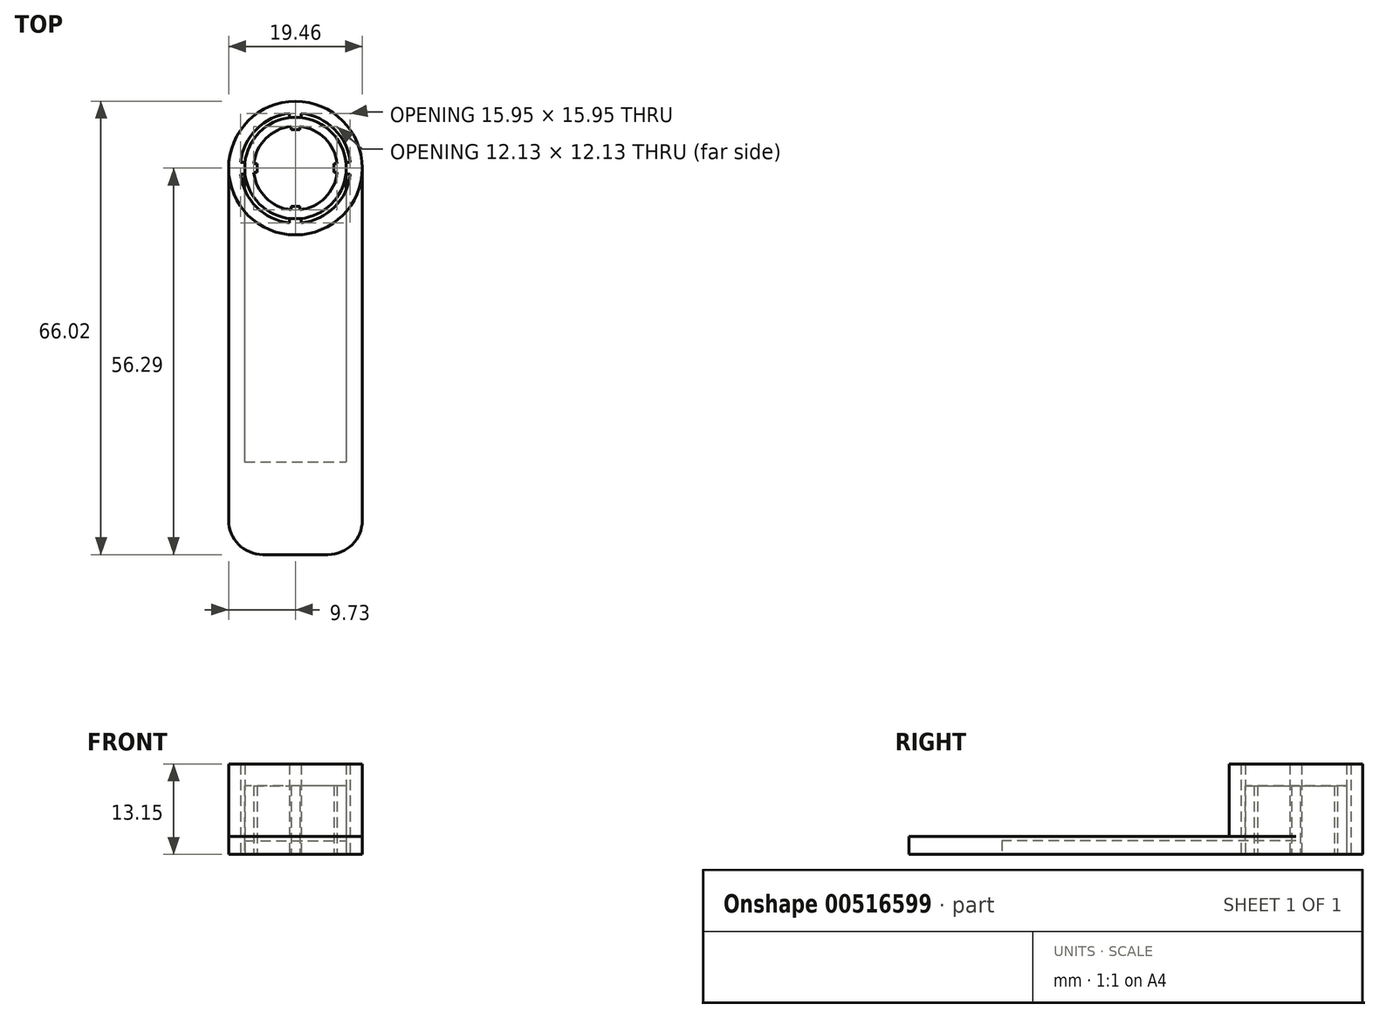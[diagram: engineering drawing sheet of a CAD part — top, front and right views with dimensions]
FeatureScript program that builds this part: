
annotation { "Feature Type Name" : "Feature", "Feature Type Description" : "" }
export const myFeature = defineFeature(function(context is Context, id is Id, definition is map)
    precondition{}
    {
        {
            var Q0;
            Q0=qCreatedBy(makeId("Top.planeOp"),FACE);
            var sketch = newSketch(context, id + "F0", { "sketchPlane" : qUnion([Q0])});
            skArc(sketch, "E0", {"start": v(0.65, -6.07) * mm, "mid": v(4.31, -4.31) * mm, "end": v(6.07, -0.65) * mm});
            skLineSegment(sketch, "E1.bottom", {"start": v(0.65, 5.6) * mm, "end": v(-0.65, 5.6) * mm});
            skLineSegment(sketch, "E1.left", {"start": v(0.65, 5.6) * mm, "end": v(0.65, 6.07) * mm});
            skLineSegment(sketch, "E1.right", {"start": v(-0.65, 5.6) * mm, "end": v(-0.65, 6.07) * mm});
            skPoint(sketch, "E1.middle", {"position": v(0, 6.1) * mm});
            skLineSegment(sketch, "E2.top", {"start": v(0.65, -5.6) * mm, "end": v(-0.65, -5.6) * mm});
            skLineSegment(sketch, "E2.left", {"start": v(0.65, -6.07) * mm, "end": v(0.65, -5.6) * mm});
            skLineSegment(sketch, "E2.right", {"start": v(-0.65, -6.07) * mm, "end": v(-0.65, -5.6) * mm});
            skPoint(sketch, "E2.middle", {"position": v(0, -6.1) * mm});
            skLineSegment(sketch, "E3.bottom", {"start": v(-6.07, -0.65) * mm, "end": v(-5.6, -0.65) * mm});
            skLineSegment(sketch, "E3.top", {"start": v(-6.07, 0.65) * mm, "end": v(-5.6, 0.65) * mm});
            skLineSegment(sketch, "E3.right", {"start": v(-5.6, -0.65) * mm, "end": v(-5.6, 0.65) * mm});
            skPoint(sketch, "E3.middle", {"position": v(-6.1, 0) * mm});
            skLineSegment(sketch, "E4.bottom", {"start": v(6.07, -0.65) * mm, "end": v(5.6, -0.65) * mm});
            skLineSegment(sketch, "E4.top", {"start": v(6.07, 0.65) * mm, "end": v(5.6, 0.65) * mm});
            skLineSegment(sketch, "E4.right", {"start": v(5.6, -0.65) * mm, "end": v(5.6, 0.65) * mm});
            skPoint(sketch, "E4.middle", {"position": v(6.1, 0) * mm});
            skCircle(sketch, "E5", {"center": v(0, 0) * mm, "radius": 7.4 * mm});
            skLineSegment(sketch, "E6.top", {"start": v(-7.4, -42.8) * mm, "end": v(7.4, -42.8) * mm});
            skLineSegment(sketch, "E6.left", {"start": v(-7.4, 0) * mm, "end": v(-7.4, -42.8) * mm});
            skLineSegment(sketch, "E6.right", {"start": v(7.4, 0) * mm, "end": v(7.4, -42.8) * mm});
            skArc(sketch, "E7.trimOffspring", {"start": v(6.07, 0.65) * mm, "mid": v(4.31, 4.31) * mm, "end": v(0.65, 6.07) * mm});
            skArc(sketch, "E8.trimOffspring", {"start": v(-0.65, 6.07) * mm, "mid": v(-4.31, 4.31) * mm, "end": v(-6.07, 0.65) * mm});
            skArc(sketch, "E9.trimOffspring", {"start": v(-6.07, -0.65) * mm, "mid": v(-4.31, -4.31) * mm, "end": v(-0.65, -6.07) * mm});
            skSolve(sketch);
        }
        {
            var Q0;
            Q0=makeQuery(id+"F0.imprint","IMPRINT",FACE,{"disambiguationData":[TD([[makeQuery(id+"F0.imprint","IMPRINT",EDGE,{"derivedFrom":sQuery(id+"F0.wireOp",EDGE,"E6.top")}),1.0]])]});
            extrude(context, id + "F1", {"entities" : qUnion([Q0]), "depth" : 2 * mm, "offsetDistance" : 25 * mm});
        }
        {
            var Q0;
            Q0=makeQuery(id+"F0.imprint","IMPRINT",FACE,{"disambiguationData":[TD([[makeQuery(id+"F0.imprint","IMPRINT",EDGE,{"derivedFrom":sQuery(id+"F0.wireOp",EDGE,"E0")}),-1.0]])]});
            extrude(context, id + "F2", {"entities" : qUnion([Q0]), "operationType" : NewBodyOperationType.ADD, "depth" : 10 * mm, "offsetDistance" : 25 * mm});
        }
        {
            var Q0;
            Q0=makeQuery(id+"F1.opExtrude","SWEPT_BODY",BODY,{"disambiguationData":[OSD([sQuery(id+"F0.wireOp",EDGE,"E5"),sQuery(id+"F0.wireOp",EDGE,"E6.top"),sQuery(id+"F0.wireOp",EDGE,"E6.left"),sQuery(id+"F0.wireOp",EDGE,"E6.right")])]});
            var Q1;
            Q1=sQuery(id+"F0.wireOp",VERTEX,"E0.center");
            transform(context, id + "F3", {"entities" : qUnion([Q0]), "transformType" : TransformType.SCALE_UNIFORMLY, "scale" : 1.31, "scalePoint" : qUnion([Q1]), "makeCopy" : true});
        }
        {
            var Q0;
            Q0=makeQuery(id+"F3.opPattern","COPY",EDGE,{"derivedFrom":makeQuery(id+"F1.opExtrude","SWEPT_EDGE",EDGE,{"disambiguationData":[OSD([sQuery(id+"F0.wireOp",EDGE,"E6.top"),sQuery(id+"F0.wireOp",EDGE,"E6.left")])]}),"instanceName":"1"});
            var Q1;
            Q1=makeQuery(id+"F3.opPattern","COPY",EDGE,{"derivedFrom":makeQuery(id+"F1.opExtrude","SWEPT_EDGE",EDGE,{"disambiguationData":[OSD([sQuery(id+"F0.wireOp",EDGE,"E6.top"),sQuery(id+"F0.wireOp",EDGE,"E6.right")])]}),"instanceName":"1"});
            fillet(context, id + "F4", {"entities" : qUnion([Q0, Q1]), "radius" : 5 * mm, "tangentPropagation" : true, "allowEdgeOverflow" : false});
        }
    });
